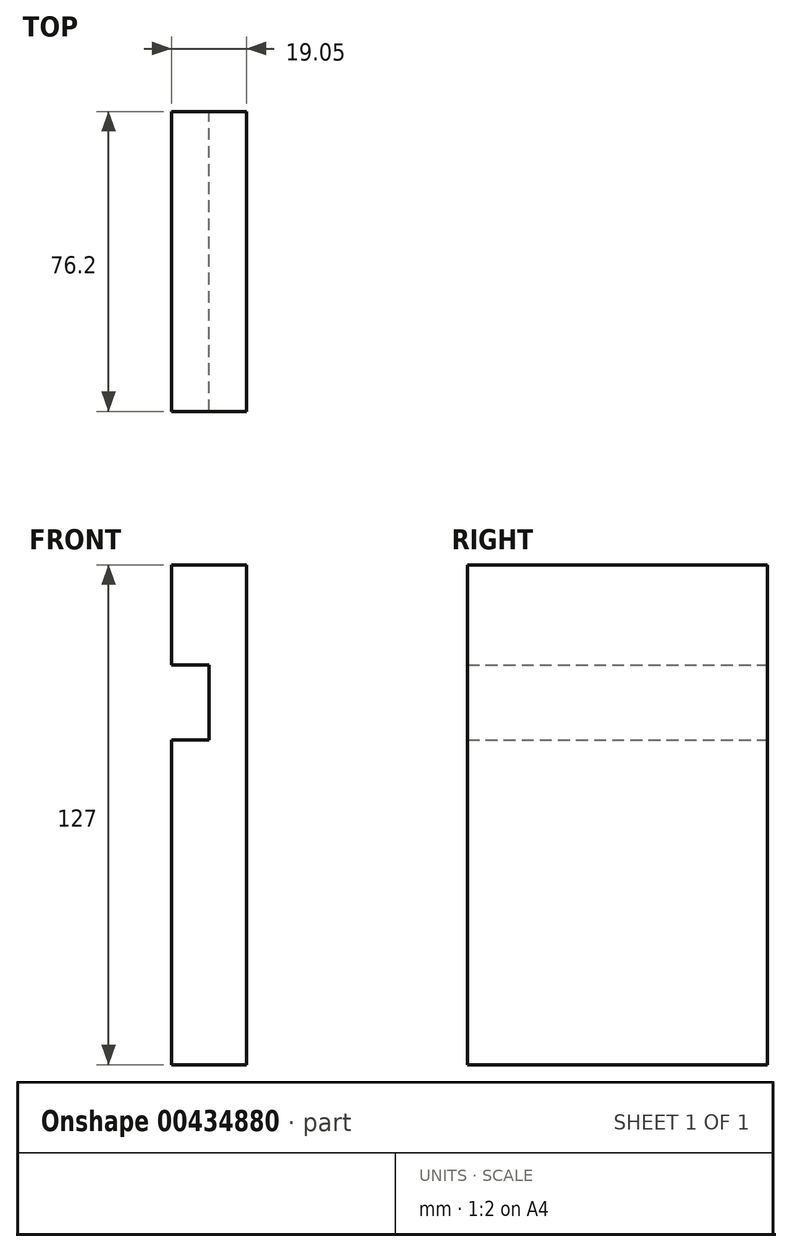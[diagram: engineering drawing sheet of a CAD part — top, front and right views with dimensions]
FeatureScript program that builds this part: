
annotation { "Feature Type Name" : "Feature", "Feature Type Description" : "" }
export const myFeature = defineFeature(function(context is Context, id is Id, definition is map)
    precondition{}
    {
        {
            var Q0;
            Q0=qCreatedBy(makeId("Front.planeOp"),FACE);
            var sketch = newSketch(context, id + "F0", { "sketchPlane" : qUnion([Q0])});
            skLineSegment(sketch, "E0", {"start": v(0, -56.52) * mm, "end": v(19.05, -56.52) * mm});
            skLineSegment(sketch, "E1", {"start": v(19.05, -56.52) * mm, "end": v(19.05, 70.48) * mm});
            skLineSegment(sketch, "E2", {"start": v(19.05, 70.48) * mm, "end": v(0, 70.48) * mm});
            skLineSegment(sketch, "E3", {"start": v(0, 70.48) * mm, "end": v(0, 45.08) * mm});
            skLineSegment(sketch, "E4", {"start": v(0, 45.08) * mm, "end": v(9.53, 45.08) * mm});
            skLineSegment(sketch, "E5", {"start": v(9.53, 45.08) * mm, "end": v(9.53, 26.03) * mm});
            skLineSegment(sketch, "E6", {"start": v(9.53, 26.03) * mm, "end": v(0, 26.03) * mm});
            skLineSegment(sketch, "E7", {"start": v(0, 26.03) * mm, "end": v(0, -56.52) * mm});
            skSolve(sketch);
        }
        {
            var Q0;
            Q0=makeQuery(id+"F0.imprint","IMPRINT",FACE,{"disambiguationData":[TD([[makeQuery(id+"F0.imprint","IMPRINT",EDGE,{"derivedFrom":sQuery(id+"F0.wireOp",EDGE,"E0")}),1.0]])]});
            extrude(context, id + "F1", {"entities" : qUnion([Q0]), "depth" : 76.2 * mm});
        }
    });
